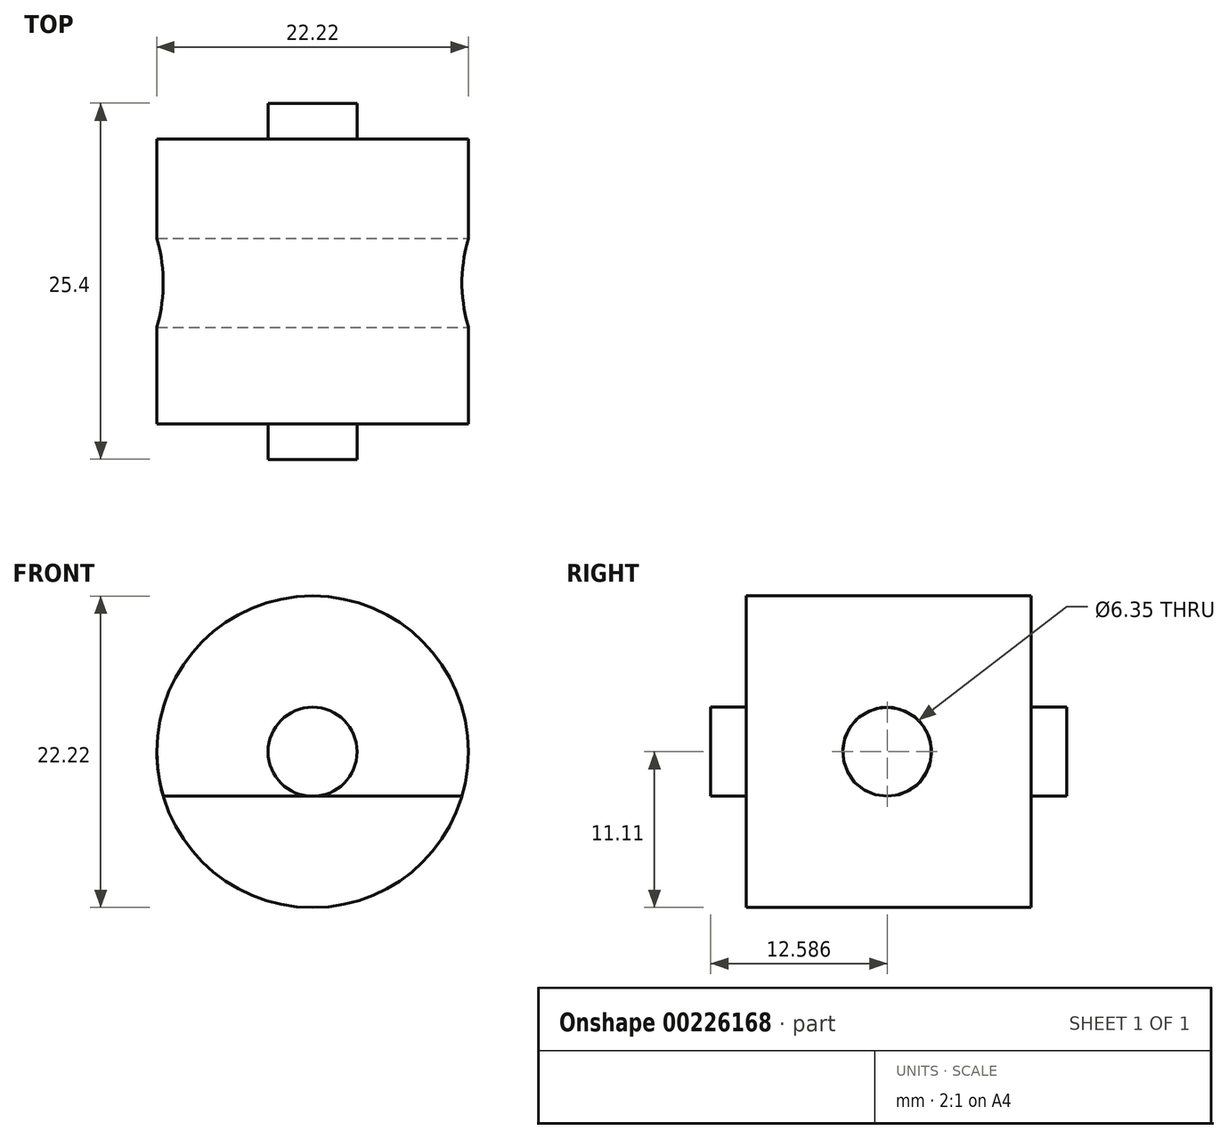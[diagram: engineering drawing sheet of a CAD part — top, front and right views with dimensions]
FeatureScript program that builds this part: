
annotation { "Feature Type Name" : "Feature", "Feature Type Description" : "" }
export const myFeature = defineFeature(function(context is Context, id is Id, definition is map)
    precondition{}
    {
        {
            var Q0;
            Q0=qCreatedBy(makeId("Right.planeOp"),FACE);
            var sketch = newSketch(context, id + "F0", { "sketchPlane" : qUnion([Q0])});
            skLineSegment(sketch, "E0", {"start": v(-11.86, 0) * mm, "end": v(13.54, 0) * mm});
            skLineSegment(sketch, "E1", {"start": v(13.54, 0) * mm, "end": v(13.54, 3.18) * mm});
            skLineSegment(sketch, "E2", {"start": v(13.54, 3.18) * mm, "end": v(11, 3.18) * mm});
            skLineSegment(sketch, "E3", {"start": v(11, 3.18) * mm, "end": v(11, 11.11) * mm});
            skLineSegment(sketch, "E4", {"start": v(11, 11.11) * mm, "end": v(-9.32, 11.11) * mm});
            skLineSegment(sketch, "E5", {"start": v(-9.32, 11.11) * mm, "end": v(-9.32, 3.18) * mm});
            skLineSegment(sketch, "E6", {"start": v(-9.32, 3.18) * mm, "end": v(-11.86, 3.18) * mm});
            skLineSegment(sketch, "E7", {"start": v(-11.86, 3.18) * mm, "end": v(-11.86, 0) * mm});
            skLineSegment(sketch, "E8", {"start": v(-54.05, 0) * mm, "end": v(60.04, 0) * mm, "construction": true});
            skSolve(sketch);
        }
        {
            var Q0;
            Q0=makeQuery(id+"F0.imprint","IMPRINT",FACE,{"disambiguationData":[TD([[makeQuery(id+"F0.imprint","IMPRINT",EDGE,{"derivedFrom":sQuery(id+"F0.wireOp",EDGE,"E0")}),1.0]])]});
            var Q1;
            Q1=sQuery(id+"F0.wireOp",EDGE,"E8");
            revolve(context, id + "F1", {"entities" : qUnion([Q0]), "axis" : qUnion([Q1]), "revolveType" : RevolveType.FULL});
        }
        {
            var Q0;
            Q0=qCreatedBy(makeId("Right.planeOp"),FACE);
            var sketch = newSketch(context, id + "F2", { "sketchPlane" : qUnion([Q0])});
            skCircle(sketch, "E9", {"center": v(0.73, 0) * mm, "radius": 3.18 * mm});
            skPoint(sketch, "E9.centerSnap0", {"position": v(0.73, 0.05) * mm});
            skSolve(sketch);
        }
        {
            var Q0;
            Q0 = qSketchRegion(id + "F2", true);
            extrude(context, id + "F3", {"entities" : qUnion([Q0]), "operationType" : NewBodyOperationType.REMOVE, "endBound" : BoundingType.SYMMETRIC, "oppositeDirection" : true, "depth" : 38.1 * mm});
        }
    });
